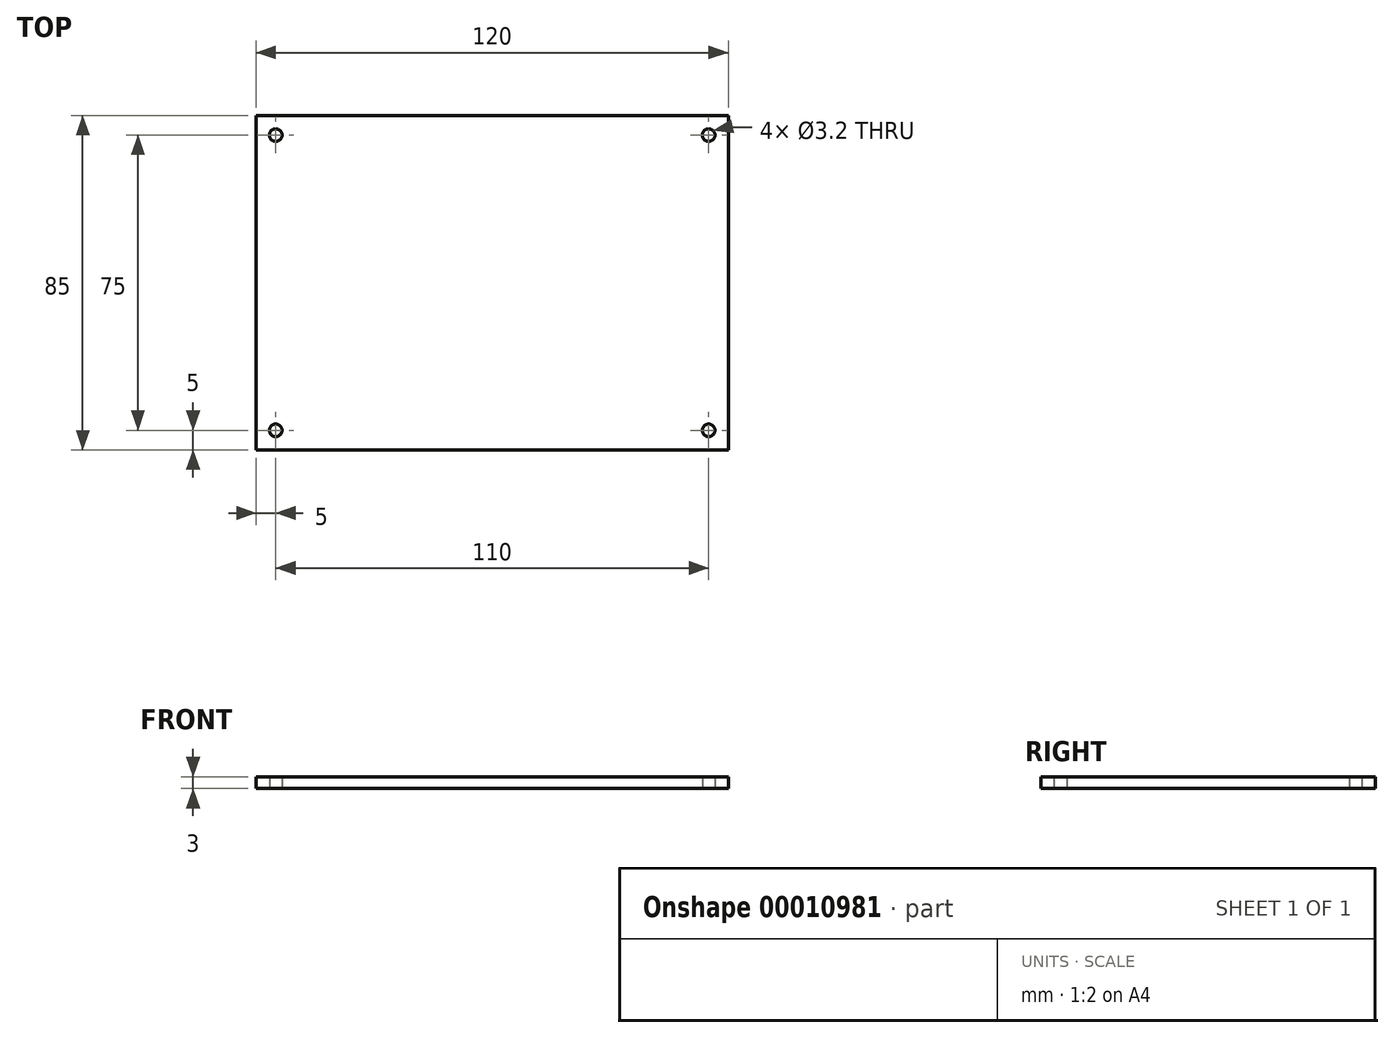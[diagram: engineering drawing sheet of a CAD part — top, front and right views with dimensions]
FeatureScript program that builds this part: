
annotation { "Feature Type Name" : "Feature", "Feature Type Description" : "" }
export const myFeature = defineFeature(function(context is Context, id is Id, definition is map)
    precondition{}
    {
        {
            var Q0;
            Q0=qCreatedBy(makeId("Top.planeOp"),FACE);
            var sketch = newSketch(context, id + "F0", { "sketchPlane" : qUnion([Q0])});
            skLineSegment(sketch, "E0.rect.bottom", {"start": v(60, 42.5) * mm, "end": v(-60, 42.5) * mm});
            skLineSegment(sketch, "E0.rect.top", {"start": v(60, -42.5) * mm, "end": v(-60, -42.5) * mm});
            skLineSegment(sketch, "E0.rect.left", {"start": v(60, 42.5) * mm, "end": v(60, -42.5) * mm});
            skLineSegment(sketch, "E0.rect.right", {"start": v(-60, 42.5) * mm, "end": v(-60, -42.5) * mm});
            skPoint(sketch, "E0.rect.middle", {"position": v(0, 0) * mm});
            skCircle(sketch, "E1", {"center": v(-55, 37.5) * mm, "radius": 1.6 * mm});
            skCircle(sketch, "E2.0.1.0", {"center": v(-55, -37.5) * mm, "radius": 1.6 * mm});
            skCircle(sketch, "E2.1.0.0", {"center": v(55, 37.5) * mm, "radius": 1.6 * mm});
            skCircle(sketch, "E2.1.1.0", {"center": v(55, -37.5) * mm, "radius": 1.6 * mm});
            skLineSegment(sketch, "E2.direction1", {"start": v(-55, 37.5) * mm, "end": v(55, 37.5) * mm, "construction": true});
            skLineSegment(sketch, "E2.direction2", {"start": v(-55, 37.5) * mm, "end": v(-55, -37.5) * mm, "construction": true});
            skSolve(sketch);
        }
        {
            var Q0;
            Q0 = qSketchRegion(id + "F0", true);
            extrude(context, id + "F1", {"entities" : qUnion([Q0]), "depth" : 3 * mm});
        }
    });
